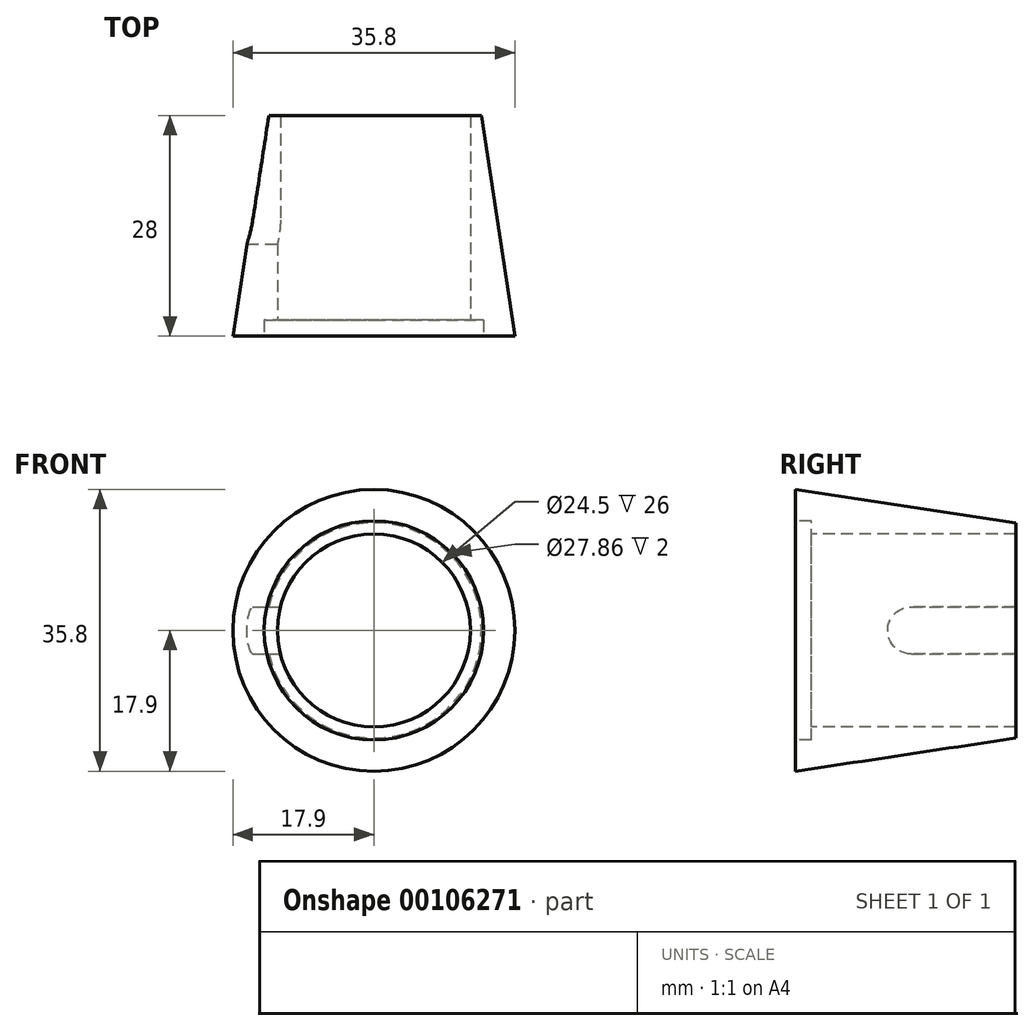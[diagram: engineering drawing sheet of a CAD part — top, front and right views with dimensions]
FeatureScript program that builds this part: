
annotation { "Feature Type Name" : "Feature", "Feature Type Description" : "" }
export const myFeature = defineFeature(function(context is Context, id is Id, definition is map)
    precondition{}
    {
        {
            var Q0;
            Q0=qCreatedBy(makeId("Right.planeOp"),FACE);
            var sketch = newSketch(context, id + "F0", { "sketchPlane" : qUnion([Q0])});
            skLineSegment(sketch, "E0", {"start": v(0, 0) * mm, "end": v(0, 3.97) * mm});
            skLineSegment(sketch, "E1", {"start": v(0, 3.97) * mm, "end": v(2, 3.97) * mm});
            skLineSegment(sketch, "E2", {"start": v(2, 3.97) * mm, "end": v(2, 5.65) * mm});
            skLineSegment(sketch, "E3", {"start": v(2, 5.65) * mm, "end": v(28, 5.65) * mm});
            skLineSegment(sketch, "E4", {"start": v(28, 5.65) * mm, "end": v(28, 4.23) * mm});
            skLineSegment(sketch, "E5", {"start": v(28, 4.23) * mm, "end": v(0, 0) * mm});
            skLineSegment(sketch, "E6", {"start": v(0, 17.9) * mm, "end": v(28, 17.9) * mm, "construction": true});
            skSolve(sketch);
        }
        {
            var Q0;
            Q0=makeQuery(id+"F0.imprint","IMPRINT",FACE,{"disambiguationData":[TD([[makeQuery(id+"F0.imprint","IMPRINT",EDGE,{"derivedFrom":sQuery(id+"F0.wireOp",EDGE,"E0")}),-1.0]])]});
            var Q1;
            Q1=sQuery(id+"F0.wireOp",EDGE,"E6");
            revolve(context, id + "F1", {"entities" : qUnion([Q0]), "axis" : qUnion([Q1]), "revolveType" : RevolveType.FULL});
        }
        {
            var Q0;
            Q0=qCreatedBy(makeId("Right.planeOp"),FACE);
            var sketch = newSketch(context, id + "F2", { "sketchPlane" : qUnion([Q0])});
            skLineSegment(sketch, "E7", {"start": v(28, 20.9) * mm, "end": v(14.7, 20.9) * mm});
            skLineSegment(sketch, "E8", {"start": v(28, 20.9) * mm, "end": v(28, 14.9) * mm});
            skLineSegment(sketch, "E9", {"start": v(28, 14.9) * mm, "end": v(14.7, 14.9) * mm});
            skArc(sketch, "E10", {"start": v(14.7, 20.9) * mm, "mid": v(11.7, 17.9) * mm, "end": v(14.7, 14.9) * mm});
            skSolve(sketch);
        }
        {
            var Q0;
            Q0=makeQuery(id+"F2.imprint","IMPRINT",FACE,{"disambiguationData":[TD([[makeQuery(id+"F2.imprint","IMPRINT",EDGE,{"derivedFrom":sQuery(id+"F2.wireOp",EDGE,"E7")}),1.0]])]});
            var Q1;
            Q1=makeQuery(id+"F1.opRevolve","SWEPT_FACE",FACE,{"disambiguationData":[OSD([sQuery(id+"F0.wireOp",EDGE,"E5")])]});
            extrude(context, id + "F3", {"entities" : qUnion([Q0]), "operationType" : NewBodyOperationType.REMOVE, "endBound" : BoundingType.UP_TO_SURFACE, "oppositeDirection" : true, "endBoundEntityFace" : qUnion([Q1]), "depth" : 25.4 * mm});
        }
    });
